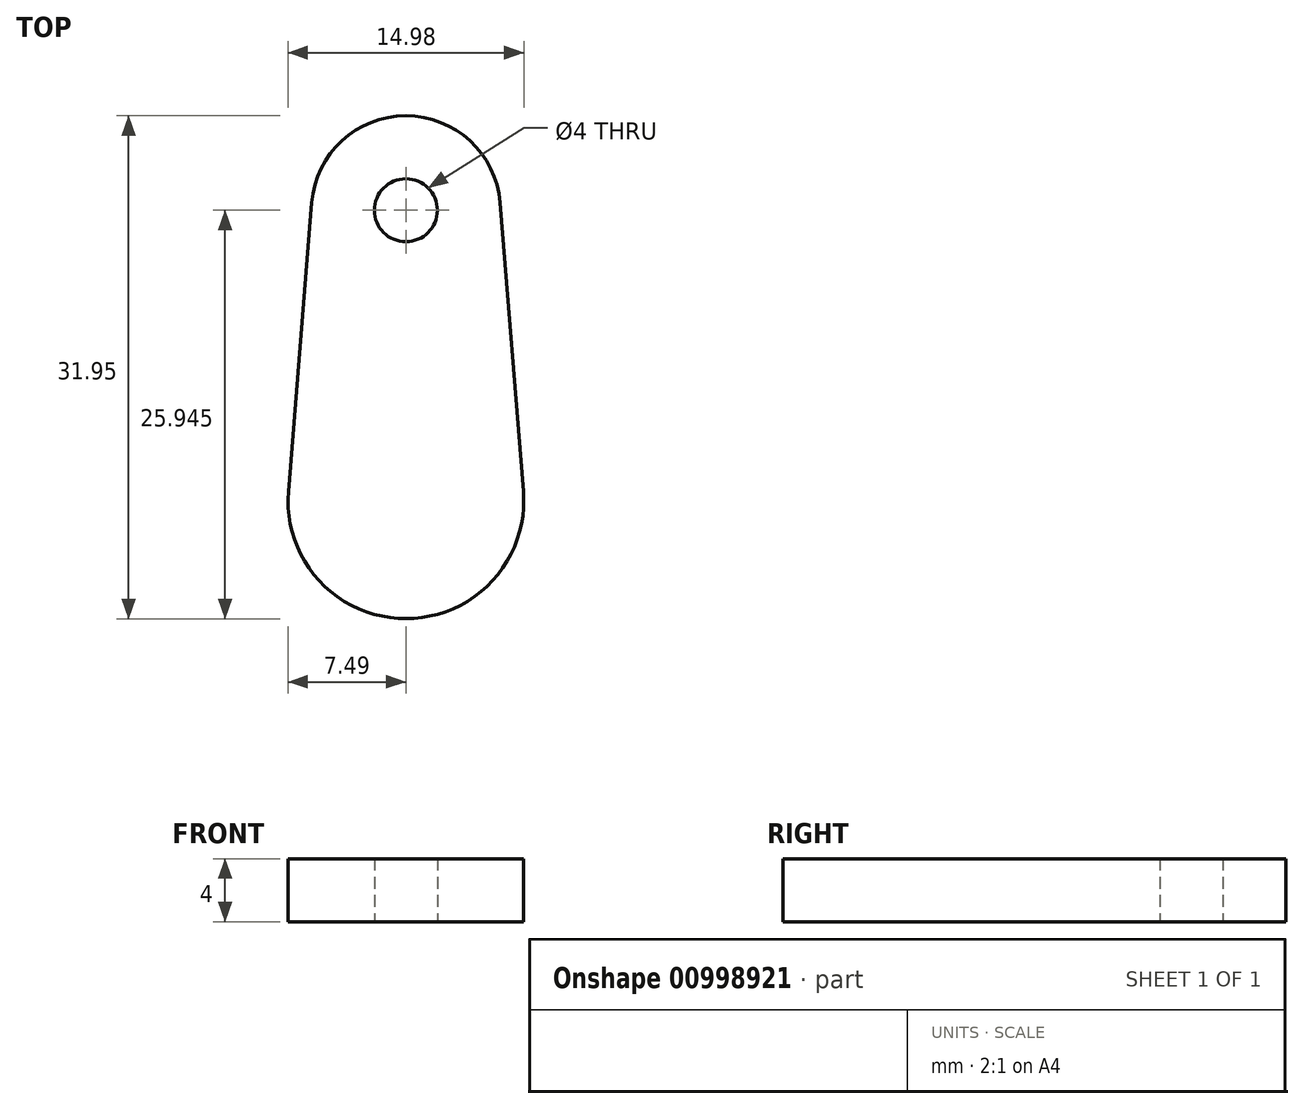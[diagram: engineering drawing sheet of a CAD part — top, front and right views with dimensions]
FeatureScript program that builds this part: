
annotation { "Feature Type Name" : "Feature", "Feature Type Description" : "" }
export const myFeature = defineFeature(function(context is Context, id is Id, definition is map)
    precondition{}
    {
        {
            var Q0;
            Q0=qCreatedBy(makeId("Top.planeOp"),FACE);
            var sketch = newSketch(context, id + "F0", { "sketchPlane" : qUnion([Q0])});
            skArc(sketch, "E0", {"start": v(5.98, 7.77) * mm, "mid": v(0, 13.29) * mm, "end": v(-5.98, 7.77) * mm});
            skArc(sketch, "E1", {"start": v(-7.46, -10.57) * mm, "mid": v(0, -18.66) * mm, "end": v(7.46, -10.57) * mm});
            skCircle(sketch, "E2", {"center": v(0, 7.29) * mm, "radius": 2 * mm});
            skLineSegment(sketch, "E3", {"start": v(-5.98, 7.77) * mm, "end": v(-7.51, -11.17) * mm});
            skLineSegment(sketch, "E4", {"start": v(5.98, 7.77) * mm, "end": v(7.51, -11.17) * mm});
            skSolve(sketch);
        }
        {
            var Q0;
            {var subQ1=sQuery(id+"F0.wireOp",EDGE,"E0");Q0=makeQuery(id+"F0.imprint","IMPRINT",FACE,{"disambiguationData":[TD([[makeQuery(id+"F0.imprint","IMPRINT",EDGE,{"derivedFrom":subQ1}),1.0]])]});}
            extrude(context, id + "F1", {"entities" : qUnion([Q0]), "depth" : 4 * mm, "offsetDistance" : 25.4 * mm});
        }
    });
